# Revit family: Haworth_ActiveComponents_StorageNook_SingleSideEnclosed_NEW
name_source: partatom
category: Furniture Systems
revit_build: Autodesk Revit Architecture 2015 (Build: 20141119_1515(x64)
units: mm (PartAtom-declared; Revit-internal decimal feet)

## types (2) — shared parameters
Actual Depth = 12"
Actual Width = 72"
Assembly Code = E2020200
Center Void = No
Custom Size = No
Divider Visibility = Yes
Manufacturer = Haworth
Max. Width = 72"
Min. Width = 24"
Model = AU1B
Mounted Height = 29"
Panel Thickness = 1/16"
Revision Number = 2
Side Void = Yes
Size = Verify Final Dim. w/ Haworth
Slot Length = 20"
Stanchion Height = 4 3/8"
Support Post Overall Width = 46"
Support Post Width = 2"
Sustainability Info = https://www.haworth.com
URL = http://www.haworth.com
URL - Product = http://www.haworth.com
Void Center Dimension = 5"
Void Side Dimension = 20"
Warranty = https://www.haworth.com
Width = 72"
With Slots = Yes

## per-type parameters (varying)
| type | Actual Height | Description | High | Low |
| 72w 14h | 14 1/4" | Haworth Active Components - Storage Nook Enclosed - Single Sided - 72w 14h | Yes | No |
| 72w 8h | 8" | Haworth Active Components - Storage Nook Enclosed - Single Sided - 72w 8h | No | Yes |

## geometry (parser evidence)
native form markers: Sweep x5
no freeform markers — native parametric forms only
